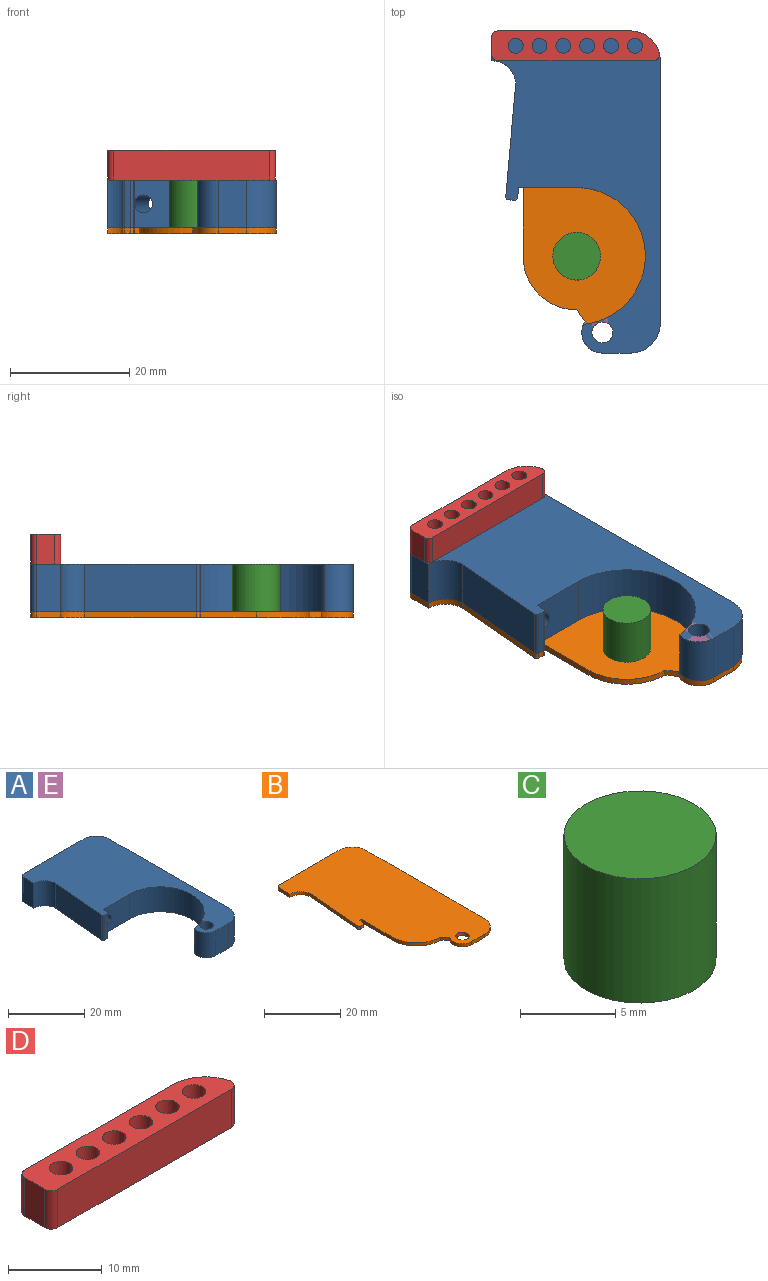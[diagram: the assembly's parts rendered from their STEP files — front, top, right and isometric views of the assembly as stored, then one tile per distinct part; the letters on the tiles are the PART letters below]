
ASSEMBLY  parts=5 mates=3
PART A: 21 faces, bbox 28.2x54x8 mm
  f0: plane 3.85x1.67mm, normal (1,-0.09,0), area 6.4mm2, adj f8,f10,f18,f20
  f1: plane 22.24x8mm, normal (0,1,0), area 170.9mm2, adj f2,f16,f18,f19,f20
  f2: cylinder r=1mm len=8mm, axis (0,0,-1), area 12.6mm2, adj f1,f3,f18,f19
  f3: plane 8x4mm, normal (-1,0,0), area 32mm2, adj f2,f4,f18,f19
  f4: cylinder r=4mm len=8mm, axis (0,0,-1), area 50.3mm2, adj f3,f5,f18,f19
  f5: plane 18.76x8mm, normal (-1,0.09,0), area 150.6mm2, adj f4,f6,f18,f19
  f6: cylinder r=0.5mm len=8mm, axis (0,0,-1), area 6.3mm2, adj f5,f7,f18,f19
  f7: plane 8x1mm, normal (-0.09,-1,0), area 8mm2, adj f6,f8,f18,f19
  f8: cylinder r=0.5mm len=8mm, axis (0,0,-1), area 6.3mm2, adj f0,f7,f9,f18,f19,f20
  f9: plane 3.85x1.67mm, normal (1,-0.09,0), area 6.4mm2, adj f8,f10,f19,f20
  f10: plane 9.76x8mm, normal (0,-1,0), area 71mm2, adj f0,f9,f11,f18,f19,f20
  f11: cylinder r=11.5mm len=22.95mm, axis (0,0,-1), area 280mm2, adj f10,f12,f18,f19
  f12: cylinder r=3.45mm len=8mm, axis (0,0,-1), area 54.5mm2, adj f11,f13,f18,f19
  f13: plane 8x4.69mm, normal (0,-1,0), area 37.5mm2, adj f12,f14,f18,f19
  f14: cylinder r=5mm len=8mm, axis (0,0,-1), area 62.8mm2, adj f13,f15,f18,f19
  f15: plane 44.01x8mm, normal (1,0,0), area 352.1mm2, adj f14,f16,f18,f19
  f16: cylinder r=5mm len=8mm, axis (0,0,-1), area 62.8mm2, adj f1,f15,f18,f19
  f17: cylinder r=1.75mm len=8mm, axis (0,0,-1), area 88mm2, adj f18,f19
  f18: plane 54.01x28.24mm, normal (0,0,1), area 830.8mm2, adj f0,f1,f2,f3,f4,f5,f6,f7
  f19: plane 54.01x28.24mm, normal (0,0,-1), area 830.8mm2, adj f1,f2,f3,f4,f5,f6,f7,f8
  f20: bspline ~27.93x5.44mm, area 249mm2, adj f0,f1,f8,f9,f10
PART B: 21 faces, bbox 28.2x54x1 mm
  f0: plane 22.24x1mm, normal (0,1,0), area 22.2mm2, adj f1,f18,f19,f20
  f1: cylinder r=1mm len=1mm, axis (0,0,-1), area 1.6mm2, adj f0,f2,f19,f20
  f2: plane 4x1mm, normal (-1,0,0), area 4mm2, adj f1,f3,f19,f20
  f3: cylinder r=4mm len=4mm, axis (0,0,-1), area 6.3mm2, adj f2,f4,f19,f20
  f4: plane 18.76x1.66mm, normal (-1,0.09,0), area 18.8mm2, adj f3,f5,f19,f20
  f5: cylinder r=0.5mm len=1mm, axis (0,0,-1), area 0.8mm2, adj f4,f6,f19,f20
  f6: plane 1x1mm, normal (-0.09,-1,0), area 1mm2, adj f5,f7,f19,f20
  f7: cylinder r=0.5mm len=1mm, axis (0,0,-1), area 0.8mm2, adj f6,f8,f19,f20
  f8: plane 1.67x1mm, normal (1,-0.09,0), area 1.7mm2, adj f7,f9,f19,f20
  f9: plane 1x0.76mm, normal (0,-1,0), area 0.8mm2, adj f8,f10,f19,f20
  f10: plane 11.5x1mm, normal (-1,0,0), area 11.5mm2, adj f9,f11,f19,f20
  f11: cylinder r=9mm len=9mm, axis (0,0,-1), area 14.1mm2, adj f10,f12,f19,f20
  f12: plane 1.91x1.41mm, normal (-0.8,-0.59,0), area 2.4mm2, adj f11,f13,f19,f20
  f13: cylinder r=3.45mm len=5.33mm, axis (0,0,-1), area 7.4mm2, adj f12,f14,f19,f20
  f14: plane 4.69x1mm, normal (0,-1,0), area 4.7mm2, adj f13,f15,f19,f20
  f15: cylinder r=5mm len=5mm, axis (0,0,-1), area 7.9mm2, adj f14,f16,f19,f20
  f16: plane 44.01x1mm, normal (1,0,0), area 44mm2, adj f15,f18,f19,f20
  f17: cylinder r=1.75mm len=3.5mm, axis (0,0,-1), area 11mm2, adj f19,f20
  f18: cylinder r=5mm len=5mm, axis (0,0,-1), area 7.9mm2, adj f0,f16,f19,f20
  f19: plane 54.01x28.24mm, normal (0,0,1), area 1203.6mm2, adj f0,f1,f2,f3,f4,f5,f6,f7
  f20: plane 54.01x28.24mm, normal (0,0,-1), area 1203.6mm2, adj f0,f1,f2,f3,f4,f5,f6,f7
PART C: 3 faces, bbox 8x8x8 mm
  f0: cylinder r=4mm len=8mm, axis (0,0,-1), area 201.1mm2, adj f1,f2
  f1: plane 8x8mm, normal (0,0,1), area 50.3mm2, adj f0
  f2: plane 8x8mm, normal (0,0,-1), area 50.3mm2, adj f0
PART D: 15 faces, bbox 28.1x5x5 mm
  f0: plane 22.24x5mm, normal (0,1,0), area 111.2mm2, adj f1,f12,f13,f14
  f1: cylinder r=1mm len=5mm, axis (0,0,-1), area 7.9mm2, adj f0,f2,f13,f14
  f2: plane 5x3mm, normal (-1,0,0), area 15mm2, adj f1,f3,f13,f14
  f3: cylinder r=1mm len=5mm, axis (0,0,-1), area 7.9mm2, adj f2,f4,f13,f14
  f4: plane 26.12x5mm, normal (0,-1,0), area 130.6mm2, adj f3,f5,f13,f14
  f5: cylinder r=1mm len=5mm, axis (0,0,-1), area 9.1mm2, adj f4,f12,f13,f14
  f6: cylinder r=1.25mm len=5mm, axis (0,0,-1), area 39.3mm2, adj f13,f14
  f7: cylinder r=1.25mm len=5mm, axis (0,0,-1), area 39.3mm2, adj f13,f14
  f8: cylinder r=1.25mm len=5mm, axis (0,0,-1), area 39.3mm2, adj f13,f14
  f9: cylinder r=1.25mm len=5mm, axis (0,0,-1), area 39.3mm2, adj f13,f14
  f10: cylinder r=1.25mm len=5mm, axis (0,0,-1), area 39.3mm2, adj f13,f14
  f11: cylinder r=1.25mm len=5mm, axis (0,0,-1), area 39.3mm2, adj f13,f14
  f12: cylinder r=5mm len=5mm, axis (0,0,-1), area 33mm2, adj f0,f5,f13,f14
  f13: plane 28.12x5mm, normal (0,0,1), area 105.7mm2, adj f0,f1,f2,f3,f4,f5,f6,f7
  f14: plane 28.12x5mm, normal (0,0,-1), area 105.7mm2, adj f0,f1,f2,f3,f4,f5,f6,f7
PART E: same geometry as A
PLACE A t=(11.35,13.69,10.59)mm
PLACE B t=(-35.5,-17.32,9.59)mm
PLACE C t=(49.57,0.73,10.59)mm
PLACE D t=(96,-39.39,18.59)mm
PLACE E t=(11.35,13.69,10.59)mm
MATE fastened D.f1 <-> A.f2  axis (0,0,-1) through (8.05,46.69,18.59)mm
MATE fastened C.f0 <-> B.f11  axis (0,0,-1) through (21.29,9.92,10.59)mm
MATE fastened A.f12 <-> B.f13  axis (0,0,-1) through (25.6,-2.87,10.59)mm
